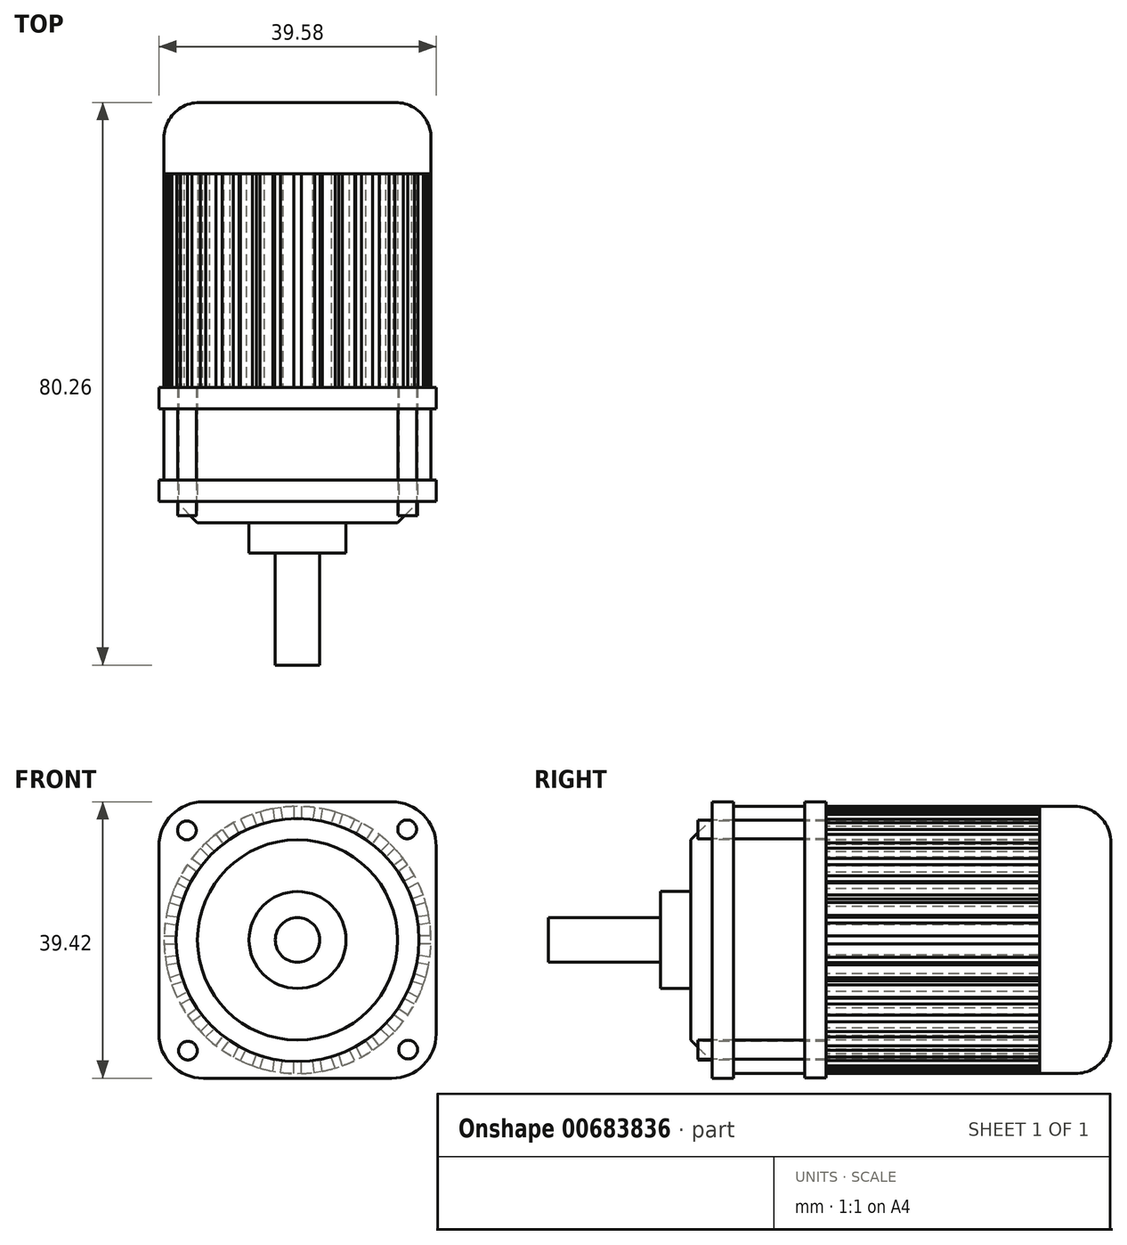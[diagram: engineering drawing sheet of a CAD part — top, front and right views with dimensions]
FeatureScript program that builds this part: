
annotation { "Feature Type Name" : "Feature", "Feature Type Description" : "" }
export const myFeature = defineFeature(function(context is Context, id is Id, definition is map)
    precondition{}
    {
        {
            var Q0;
            Q0=qCreatedBy(makeId("Front.planeOp"),FACE);
            var sketch = newSketch(context, id + "F0", { "sketchPlane" : qUnion([Q0])});
            skCircle(sketch, "E0", {"center": v(0, 0) * mm, "radius": 19.05 * mm});
            skSolve(sketch);
        }
        {
            var Q0;
            Q0=makeQuery(id+"F0.imprint","IMPRINT",FACE,{"disambiguationData":[TD([[makeQuery(id+"F0.imprint","IMPRINT",EDGE,{"derivedFrom":sQuery(id+"F0.wireOp",EDGE,"E0")}),1.0]])]});
            extrude(context, id + "F1", {"entities" : qUnion([Q0]), "depth" : 15.24 * mm, "offsetDistance" : 25.4 * mm, "hasSecondDirection" : true, "secondDirectionOppositeDirection" : true, "secondDirectionDepth" : 15.24 * mm});
        }
        {
            var Q0;
            Q0=makeQuery(id+"F1.opExtrude","CAP_FACE",FACE,{"disambiguationData":[OSD([sQuery(id+"F0.wireOp",EDGE,"E0")])],"isStart":false});
            var sketch = newSketch(context, id + "F2", { "sketchPlane" : qUnion([Q0])});
            skLineSegment(sketch, "E1.bottom", {"start": v(-0.55, 19.72) * mm, "end": v(0.56, 19.72) * mm});
            skLineSegment(sketch, "E1.top", {"start": v(-0.55, 17.23) * mm, "end": v(0.56, 17.23) * mm});
            skLineSegment(sketch, "E1.left", {"start": v(-0.55, 19.72) * mm, "end": v(-0.55, 17.23) * mm});
            skLineSegment(sketch, "E1.right", {"start": v(0.56, 19.72) * mm, "end": v(0.56, 17.23) * mm});
            skLineSegment(sketch, "E2.1.0", {"start": v(3.64, 19.39) * mm, "end": v(3.25, 16.94) * mm});
            skLineSegment(sketch, "E2.1.1", {"start": v(2.54, 19.56) * mm, "end": v(3.64, 19.39) * mm});
            skLineSegment(sketch, "E2.1.2", {"start": v(2.15, 17.1) * mm, "end": v(3.25, 16.94) * mm});
            skLineSegment(sketch, "E2.1.3", {"start": v(2.54, 19.56) * mm, "end": v(2.15, 17.1) * mm});
            skLineSegment(sketch, "E2.2.0", {"start": v(6.62, 18.58) * mm, "end": v(5.86, 16.22) * mm});
            skLineSegment(sketch, "E2.2.1", {"start": v(5.57, 18.92) * mm, "end": v(6.62, 18.58) * mm});
            skLineSegment(sketch, "E2.2.2", {"start": v(4.8, 16.56) * mm, "end": v(5.86, 16.22) * mm});
            skLineSegment(sketch, "E2.2.3", {"start": v(5.57, 18.92) * mm, "end": v(4.8, 16.56) * mm});
            skLineSegment(sketch, "E2.3.0", {"start": v(9.45, 17.31) * mm, "end": v(8.32, 15.1) * mm});
            skLineSegment(sketch, "E2.3.1", {"start": v(8.46, 17.82) * mm, "end": v(9.45, 17.31) * mm});
            skLineSegment(sketch, "E2.3.2", {"start": v(7.33, 15.6) * mm, "end": v(8.32, 15.1) * mm});
            skLineSegment(sketch, "E2.3.3", {"start": v(8.46, 17.82) * mm, "end": v(7.33, 15.6) * mm});
            skLineSegment(sketch, "E2.4.0", {"start": v(12.04, 15.62) * mm, "end": v(10.58, 13.62) * mm});
            skLineSegment(sketch, "E2.4.1", {"start": v(11.14, 16.28) * mm, "end": v(12.04, 15.62) * mm});
            skLineSegment(sketch, "E2.4.2", {"start": v(9.68, 14.27) * mm, "end": v(10.58, 13.62) * mm});
            skLineSegment(sketch, "E2.4.3", {"start": v(11.14, 16.28) * mm, "end": v(9.68, 14.27) * mm});
            skLineSegment(sketch, "E2.5.0", {"start": v(14.34, 13.55) * mm, "end": v(12.58, 11.8) * mm});
            skLineSegment(sketch, "E2.5.1", {"start": v(13.55, 14.33) * mm, "end": v(14.34, 13.55) * mm});
            skLineSegment(sketch, "E2.5.2", {"start": v(11.8, 12.58) * mm, "end": v(12.58, 11.8) * mm});
            skLineSegment(sketch, "E2.5.3", {"start": v(13.55, 14.33) * mm, "end": v(11.8, 12.58) * mm});
            skLineSegment(sketch, "E2.6.0", {"start": v(16.28, 11.14) * mm, "end": v(14.27, 9.68) * mm});
            skLineSegment(sketch, "E2.6.1", {"start": v(15.63, 12.04) * mm, "end": v(16.28, 11.14) * mm});
            skLineSegment(sketch, "E2.6.2", {"start": v(13.62, 10.58) * mm, "end": v(14.27, 9.68) * mm});
            skLineSegment(sketch, "E2.6.3", {"start": v(15.63, 12.04) * mm, "end": v(13.62, 10.58) * mm});
            skLineSegment(sketch, "E2.7.0", {"start": v(17.82, 8.45) * mm, "end": v(15.6, 7.33) * mm});
            skLineSegment(sketch, "E2.7.1", {"start": v(17.32, 9.44) * mm, "end": v(17.82, 8.45) * mm});
            skLineSegment(sketch, "E2.7.2", {"start": v(15.1, 8.32) * mm, "end": v(15.6, 7.33) * mm});
            skLineSegment(sketch, "E2.7.3", {"start": v(17.32, 9.44) * mm, "end": v(15.1, 8.32) * mm});
            skLineSegment(sketch, "E2.8.0", {"start": v(18.92, 5.56) * mm, "end": v(16.56, 4.8) * mm});
            skLineSegment(sketch, "E2.8.1", {"start": v(18.58, 6.62) * mm, "end": v(18.92, 5.56) * mm});
            skLineSegment(sketch, "E2.8.2", {"start": v(16.22, 5.85) * mm, "end": v(16.56, 4.8) * mm});
            skLineSegment(sketch, "E2.8.3", {"start": v(18.58, 6.62) * mm, "end": v(16.22, 5.85) * mm});
            skLineSegment(sketch, "E2.9.0", {"start": v(19.56, 2.53) * mm, "end": v(17.11, 2.14) * mm});
            skLineSegment(sketch, "E2.9.1", {"start": v(19.39, 3.63) * mm, "end": v(19.56, 2.53) * mm});
            skLineSegment(sketch, "E2.9.2", {"start": v(16.94, 3.24) * mm, "end": v(17.11, 2.14) * mm});
            skLineSegment(sketch, "E2.9.3", {"start": v(19.39, 3.63) * mm, "end": v(16.94, 3.24) * mm});
            skLineSegment(sketch, "E2.10.0", {"start": v(19.72, -0.56) * mm, "end": v(17.23, -0.56) * mm});
            skLineSegment(sketch, "E2.10.1", {"start": v(19.72, 0.55) * mm, "end": v(19.72, -0.56) * mm});
            skLineSegment(sketch, "E2.10.2", {"start": v(17.23, 0.55) * mm, "end": v(17.23, -0.56) * mm});
            skLineSegment(sketch, "E2.10.3", {"start": v(19.72, 0.55) * mm, "end": v(17.23, 0.55) * mm});
            skLineSegment(sketch, "E2.11.0", {"start": v(19.39, -3.64) * mm, "end": v(16.94, -3.25) * mm});
            skLineSegment(sketch, "E2.11.1", {"start": v(19.56, -2.54) * mm, "end": v(19.39, -3.64) * mm});
            skLineSegment(sketch, "E2.11.2", {"start": v(17.1, -2.15) * mm, "end": v(16.94, -3.25) * mm});
            skLineSegment(sketch, "E2.11.3", {"start": v(19.56, -2.54) * mm, "end": v(17.1, -2.15) * mm});
            skLineSegment(sketch, "E2.12.0", {"start": v(18.58, -6.62) * mm, "end": v(16.22, -5.86) * mm});
            skLineSegment(sketch, "E2.12.1", {"start": v(18.92, -5.57) * mm, "end": v(18.58, -6.62) * mm});
            skLineSegment(sketch, "E2.12.2", {"start": v(16.56, -4.8) * mm, "end": v(16.22, -5.86) * mm});
            skLineSegment(sketch, "E2.12.3", {"start": v(18.92, -5.57) * mm, "end": v(16.56, -4.8) * mm});
            skLineSegment(sketch, "E2.13.0", {"start": v(17.31, -9.45) * mm, "end": v(15.1, -8.32) * mm});
            skLineSegment(sketch, "E2.13.1", {"start": v(17.82, -8.46) * mm, "end": v(17.31, -9.45) * mm});
            skLineSegment(sketch, "E2.13.2", {"start": v(15.6, -7.33) * mm, "end": v(15.1, -8.32) * mm});
            skLineSegment(sketch, "E2.13.3", {"start": v(17.82, -8.46) * mm, "end": v(15.6, -7.33) * mm});
            skLineSegment(sketch, "E2.14.0", {"start": v(15.62, -12.04) * mm, "end": v(13.62, -10.58) * mm});
            skLineSegment(sketch, "E2.14.1", {"start": v(16.28, -11.14) * mm, "end": v(15.62, -12.04) * mm});
            skLineSegment(sketch, "E2.14.2", {"start": v(14.27, -9.68) * mm, "end": v(13.62, -10.58) * mm});
            skLineSegment(sketch, "E2.14.3", {"start": v(16.28, -11.14) * mm, "end": v(14.27, -9.68) * mm});
            skLineSegment(sketch, "E2.15.0", {"start": v(13.55, -14.34) * mm, "end": v(11.8, -12.58) * mm});
            skLineSegment(sketch, "E2.15.1", {"start": v(14.33, -13.55) * mm, "end": v(13.55, -14.34) * mm});
            skLineSegment(sketch, "E2.15.2", {"start": v(12.58, -11.8) * mm, "end": v(11.8, -12.58) * mm});
            skLineSegment(sketch, "E2.15.3", {"start": v(14.33, -13.55) * mm, "end": v(12.58, -11.8) * mm});
            skLineSegment(sketch, "E2.16.0", {"start": v(11.14, -16.28) * mm, "end": v(9.68, -14.27) * mm});
            skLineSegment(sketch, "E2.16.1", {"start": v(12.04, -15.63) * mm, "end": v(11.14, -16.28) * mm});
            skLineSegment(sketch, "E2.16.2", {"start": v(10.58, -13.62) * mm, "end": v(9.68, -14.27) * mm});
            skLineSegment(sketch, "E2.16.3", {"start": v(12.04, -15.63) * mm, "end": v(10.58, -13.62) * mm});
            skLineSegment(sketch, "E2.17.0", {"start": v(8.45, -17.82) * mm, "end": v(7.33, -15.6) * mm});
            skLineSegment(sketch, "E2.17.1", {"start": v(9.44, -17.32) * mm, "end": v(8.45, -17.82) * mm});
            skLineSegment(sketch, "E2.17.2", {"start": v(8.32, -15.1) * mm, "end": v(7.33, -15.6) * mm});
            skLineSegment(sketch, "E2.17.3", {"start": v(9.44, -17.32) * mm, "end": v(8.32, -15.1) * mm});
            skLineSegment(sketch, "E2.18.0", {"start": v(5.56, -18.92) * mm, "end": v(4.8, -16.56) * mm});
            skLineSegment(sketch, "E2.18.1", {"start": v(6.62, -18.58) * mm, "end": v(5.56, -18.92) * mm});
            skLineSegment(sketch, "E2.18.2", {"start": v(5.85, -16.22) * mm, "end": v(4.8, -16.56) * mm});
            skLineSegment(sketch, "E2.18.3", {"start": v(6.62, -18.58) * mm, "end": v(5.85, -16.22) * mm});
            skLineSegment(sketch, "E2.19.0", {"start": v(2.53, -19.56) * mm, "end": v(2.14, -17.11) * mm});
            skLineSegment(sketch, "E2.19.1", {"start": v(3.63, -19.39) * mm, "end": v(2.53, -19.56) * mm});
            skLineSegment(sketch, "E2.19.2", {"start": v(3.24, -16.94) * mm, "end": v(2.14, -17.11) * mm});
            skLineSegment(sketch, "E2.19.3", {"start": v(3.63, -19.39) * mm, "end": v(3.24, -16.94) * mm});
            skLineSegment(sketch, "E2.20.0", {"start": v(-0.56, -19.72) * mm, "end": v(-0.56, -17.23) * mm});
            skLineSegment(sketch, "E2.20.1", {"start": v(0.55, -19.72) * mm, "end": v(-0.56, -19.72) * mm});
            skLineSegment(sketch, "E2.20.2", {"start": v(0.55, -17.23) * mm, "end": v(-0.56, -17.23) * mm});
            skLineSegment(sketch, "E2.20.3", {"start": v(0.55, -19.72) * mm, "end": v(0.55, -17.23) * mm});
            skLineSegment(sketch, "E2.21.0", {"start": v(-3.64, -19.39) * mm, "end": v(-3.25, -16.94) * mm});
            skLineSegment(sketch, "E2.21.1", {"start": v(-2.54, -19.56) * mm, "end": v(-3.64, -19.39) * mm});
            skLineSegment(sketch, "E2.21.2", {"start": v(-2.15, -17.1) * mm, "end": v(-3.25, -16.94) * mm});
            skLineSegment(sketch, "E2.21.3", {"start": v(-2.54, -19.56) * mm, "end": v(-2.15, -17.1) * mm});
            skLineSegment(sketch, "E2.22.0", {"start": v(-6.62, -18.58) * mm, "end": v(-5.86, -16.22) * mm});
            skLineSegment(sketch, "E2.22.1", {"start": v(-5.57, -18.92) * mm, "end": v(-6.62, -18.58) * mm});
            skLineSegment(sketch, "E2.22.2", {"start": v(-4.8, -16.56) * mm, "end": v(-5.86, -16.22) * mm});
            skLineSegment(sketch, "E2.22.3", {"start": v(-5.57, -18.92) * mm, "end": v(-4.8, -16.56) * mm});
            skLineSegment(sketch, "E2.23.0", {"start": v(-9.45, -17.31) * mm, "end": v(-8.32, -15.1) * mm});
            skLineSegment(sketch, "E2.23.1", {"start": v(-8.46, -17.82) * mm, "end": v(-9.45, -17.31) * mm});
            skLineSegment(sketch, "E2.23.2", {"start": v(-7.33, -15.6) * mm, "end": v(-8.32, -15.1) * mm});
            skLineSegment(sketch, "E2.23.3", {"start": v(-8.46, -17.82) * mm, "end": v(-7.33, -15.6) * mm});
            skLineSegment(sketch, "E2.24.0", {"start": v(-12.04, -15.62) * mm, "end": v(-10.58, -13.62) * mm});
            skLineSegment(sketch, "E2.24.1", {"start": v(-11.14, -16.28) * mm, "end": v(-12.04, -15.62) * mm});
            skLineSegment(sketch, "E2.24.2", {"start": v(-9.68, -14.27) * mm, "end": v(-10.58, -13.62) * mm});
            skLineSegment(sketch, "E2.24.3", {"start": v(-11.14, -16.28) * mm, "end": v(-9.68, -14.27) * mm});
            skLineSegment(sketch, "E2.25.0", {"start": v(-14.34, -13.55) * mm, "end": v(-12.58, -11.8) * mm});
            skLineSegment(sketch, "E2.25.1", {"start": v(-13.55, -14.33) * mm, "end": v(-14.34, -13.55) * mm});
            skLineSegment(sketch, "E2.25.2", {"start": v(-11.8, -12.58) * mm, "end": v(-12.58, -11.8) * mm});
            skLineSegment(sketch, "E2.25.3", {"start": v(-13.55, -14.33) * mm, "end": v(-11.8, -12.58) * mm});
            skLineSegment(sketch, "E2.26.0", {"start": v(-16.28, -11.14) * mm, "end": v(-14.27, -9.68) * mm});
            skLineSegment(sketch, "E2.26.1", {"start": v(-15.63, -12.04) * mm, "end": v(-16.28, -11.14) * mm});
            skLineSegment(sketch, "E2.26.2", {"start": v(-13.62, -10.58) * mm, "end": v(-14.27, -9.68) * mm});
            skLineSegment(sketch, "E2.26.3", {"start": v(-15.63, -12.04) * mm, "end": v(-13.62, -10.58) * mm});
            skLineSegment(sketch, "E2.27.0", {"start": v(-17.82, -8.45) * mm, "end": v(-15.6, -7.33) * mm});
            skLineSegment(sketch, "E2.27.1", {"start": v(-17.32, -9.44) * mm, "end": v(-17.82, -8.45) * mm});
            skLineSegment(sketch, "E2.27.2", {"start": v(-15.1, -8.32) * mm, "end": v(-15.6, -7.33) * mm});
            skLineSegment(sketch, "E2.27.3", {"start": v(-17.32, -9.44) * mm, "end": v(-15.1, -8.32) * mm});
            skLineSegment(sketch, "E2.28.0", {"start": v(-18.92, -5.56) * mm, "end": v(-16.56, -4.8) * mm});
            skLineSegment(sketch, "E2.28.1", {"start": v(-18.58, -6.62) * mm, "end": v(-18.92, -5.56) * mm});
            skLineSegment(sketch, "E2.28.2", {"start": v(-16.22, -5.85) * mm, "end": v(-16.56, -4.8) * mm});
            skLineSegment(sketch, "E2.28.3", {"start": v(-18.58, -6.62) * mm, "end": v(-16.22, -5.85) * mm});
            skLineSegment(sketch, "E2.29.0", {"start": v(-19.56, -2.53) * mm, "end": v(-17.11, -2.14) * mm});
            skLineSegment(sketch, "E2.29.1", {"start": v(-19.39, -3.63) * mm, "end": v(-19.56, -2.53) * mm});
            skLineSegment(sketch, "E2.29.2", {"start": v(-16.94, -3.24) * mm, "end": v(-17.11, -2.14) * mm});
            skLineSegment(sketch, "E2.29.3", {"start": v(-19.39, -3.63) * mm, "end": v(-16.94, -3.24) * mm});
            skLineSegment(sketch, "E2.30.0", {"start": v(-19.72, 0.56) * mm, "end": v(-17.23, 0.56) * mm});
            skLineSegment(sketch, "E2.30.1", {"start": v(-19.72, -0.55) * mm, "end": v(-19.72, 0.56) * mm});
            skLineSegment(sketch, "E2.30.2", {"start": v(-17.23, -0.55) * mm, "end": v(-17.23, 0.56) * mm});
            skLineSegment(sketch, "E2.30.3", {"start": v(-19.72, -0.55) * mm, "end": v(-17.23, -0.55) * mm});
            skLineSegment(sketch, "E2.31.0", {"start": v(-19.39, 3.64) * mm, "end": v(-16.94, 3.25) * mm});
            skLineSegment(sketch, "E2.31.1", {"start": v(-19.56, 2.54) * mm, "end": v(-19.39, 3.64) * mm});
            skLineSegment(sketch, "E2.31.2", {"start": v(-17.1, 2.15) * mm, "end": v(-16.94, 3.25) * mm});
            skLineSegment(sketch, "E2.31.3", {"start": v(-19.56, 2.54) * mm, "end": v(-17.1, 2.15) * mm});
            skLineSegment(sketch, "E2.32.0", {"start": v(-18.58, 6.62) * mm, "end": v(-16.22, 5.86) * mm});
            skLineSegment(sketch, "E2.32.1", {"start": v(-18.92, 5.57) * mm, "end": v(-18.58, 6.62) * mm});
            skLineSegment(sketch, "E2.32.2", {"start": v(-16.56, 4.8) * mm, "end": v(-16.22, 5.86) * mm});
            skLineSegment(sketch, "E2.32.3", {"start": v(-18.92, 5.57) * mm, "end": v(-16.56, 4.8) * mm});
            skLineSegment(sketch, "E2.33.0", {"start": v(-17.31, 9.45) * mm, "end": v(-15.1, 8.32) * mm});
            skLineSegment(sketch, "E2.33.1", {"start": v(-17.82, 8.46) * mm, "end": v(-17.31, 9.45) * mm});
            skLineSegment(sketch, "E2.33.2", {"start": v(-15.6, 7.33) * mm, "end": v(-15.1, 8.32) * mm});
            skLineSegment(sketch, "E2.33.3", {"start": v(-17.82, 8.46) * mm, "end": v(-15.6, 7.33) * mm});
            skLineSegment(sketch, "E2.34.0", {"start": v(-15.62, 12.04) * mm, "end": v(-13.62, 10.58) * mm});
            skLineSegment(sketch, "E2.34.1", {"start": v(-16.28, 11.14) * mm, "end": v(-15.62, 12.04) * mm});
            skLineSegment(sketch, "E2.34.2", {"start": v(-14.27, 9.68) * mm, "end": v(-13.62, 10.58) * mm});
            skLineSegment(sketch, "E2.34.3", {"start": v(-16.28, 11.14) * mm, "end": v(-14.27, 9.68) * mm});
            skLineSegment(sketch, "E2.35.0", {"start": v(-13.55, 14.34) * mm, "end": v(-11.8, 12.58) * mm});
            skLineSegment(sketch, "E2.35.1", {"start": v(-14.33, 13.55) * mm, "end": v(-13.55, 14.34) * mm});
            skLineSegment(sketch, "E2.35.2", {"start": v(-12.58, 11.8) * mm, "end": v(-11.8, 12.58) * mm});
            skLineSegment(sketch, "E2.35.3", {"start": v(-14.33, 13.55) * mm, "end": v(-12.58, 11.8) * mm});
            skLineSegment(sketch, "E2.36.0", {"start": v(-11.14, 16.28) * mm, "end": v(-9.68, 14.27) * mm});
            skLineSegment(sketch, "E2.36.1", {"start": v(-12.04, 15.63) * mm, "end": v(-11.14, 16.28) * mm});
            skLineSegment(sketch, "E2.36.2", {"start": v(-10.58, 13.62) * mm, "end": v(-9.68, 14.27) * mm});
            skLineSegment(sketch, "E2.36.3", {"start": v(-12.04, 15.63) * mm, "end": v(-10.58, 13.62) * mm});
            skLineSegment(sketch, "E2.37.0", {"start": v(-8.45, 17.82) * mm, "end": v(-7.33, 15.6) * mm});
            skLineSegment(sketch, "E2.37.1", {"start": v(-9.44, 17.32) * mm, "end": v(-8.45, 17.82) * mm});
            skLineSegment(sketch, "E2.37.2", {"start": v(-8.32, 15.1) * mm, "end": v(-7.33, 15.6) * mm});
            skLineSegment(sketch, "E2.37.3", {"start": v(-9.44, 17.32) * mm, "end": v(-8.32, 15.1) * mm});
            skLineSegment(sketch, "E2.38.0", {"start": v(-5.56, 18.92) * mm, "end": v(-4.8, 16.56) * mm});
            skLineSegment(sketch, "E2.38.1", {"start": v(-6.62, 18.58) * mm, "end": v(-5.56, 18.92) * mm});
            skLineSegment(sketch, "E2.38.2", {"start": v(-5.85, 16.22) * mm, "end": v(-4.8, 16.56) * mm});
            skLineSegment(sketch, "E2.38.3", {"start": v(-6.62, 18.58) * mm, "end": v(-5.85, 16.22) * mm});
            skLineSegment(sketch, "E2.39.0", {"start": v(-2.53, 19.56) * mm, "end": v(-2.14, 17.11) * mm});
            skLineSegment(sketch, "E2.39.1", {"start": v(-3.63, 19.39) * mm, "end": v(-2.53, 19.56) * mm});
            skLineSegment(sketch, "E2.39.2", {"start": v(-3.24, 16.94) * mm, "end": v(-2.14, 17.11) * mm});
            skLineSegment(sketch, "E2.39.3", {"start": v(-3.63, 19.39) * mm, "end": v(-3.24, 16.94) * mm});
            skPoint(sketch, "E2.center", {"position": v(0, 0) * mm});
            skLineSegment(sketch, "E2.anchor1", {"start": v(0, 0) * mm, "end": v(0.56, 17.23) * mm, "construction": true});
            skLineSegment(sketch, "E2.anchor2", {"start": v(0, 0) * mm, "end": v(-2.14, 17.11) * mm, "construction": true});
            skSolve(sketch);
        }
        {
            var Q0;
            Q0 = qSketchRegion(id + "F2", true);
            extrude(context, id + "F3", {"entities" : qUnion([Q0]), "operationType" : NewBodyOperationType.REMOVE, "oppositeDirection" : true, "depth" : 35.56 * mm, "offsetDistance" : 25.4 * mm});
        }
        {
            var Q0;
            Q0=makeQuery(id+"F1.opExtrude","CAP_FACE",FACE,{"disambiguationData":[OSD([sQuery(id+"F0.wireOp",EDGE,"E0")])],"isStart":true});
            var sketch = newSketch(context, id + "F4", { "sketchPlane" : qUnion([Q0])});
            skCircle(sketch, "E3", {"center": v(0, 0) * mm, "radius": 19.05 * mm});
            skSolve(sketch);
        }
        {
            var Q0;
            Q0 = qSketchRegion(id + "F4", true);
            extrude(context, id + "F5", {"entities" : qUnion([Q0]), "depth" : 10.16 * mm, "offsetDistance" : 25.4 * mm});
        }
        {
            var Q0;
            Q0=makeQuery(id+"F5.opExtrude","CAP_FACE",FACE,{"disambiguationData":[OSD([sQuery(id+"F4.wireOp",EDGE,"E3")])],"isStart":false});
            fillet(context, id + "F6", {"entities" : qUnion([Q0]), "radius" : 5.08 * mm, "tangentPropagation" : true, "allowEdgeOverflow" : false});
        }
        {
            var Q0;
            Q0=makeQuery(id+"F1.opExtrude","CAP_FACE",FACE,{"disambiguationData":[OSD([sQuery(id+"F0.wireOp",EDGE,"E0")])],"isStart":false});
            var sketch = newSketch(context, id + "F7", { "sketchPlane" : qUnion([Q0])});
            skLineSegment(sketch, "E4.bottom", {"start": v(13.43, -19.69) * mm, "end": v(-13.43, -19.69) * mm});
            skLineSegment(sketch, "E4.top", {"start": v(13.43, 19.69) * mm, "end": v(-13.43, 19.69) * mm});
            skLineSegment(sketch, "E4.left", {"start": v(19.78, -13.34) * mm, "end": v(19.78, 13.34) * mm});
            skLineSegment(sketch, "E4.right", {"start": v(-19.78, -13.34) * mm, "end": v(-19.78, 13.34) * mm});
            skPoint(sketch, "E4.middle", {"position": v(0, 0) * mm});
            skPoint(sketch, "E5.visualSharp", {"position": v(-19.78, 19.69) * mm});
            skArc(sketch, "E5.filletArc", {"start": v(-13.43, 19.69) * mm, "mid": v(-17.92, 17.83) * mm, "end": v(-19.78, 13.34) * mm});
            skPoint(sketch, "E6.visualSharp", {"position": v(19.78, 19.69) * mm});
            skArc(sketch, "E6.filletArc", {"start": v(19.78, 13.34) * mm, "mid": v(17.92, 17.83) * mm, "end": v(13.43, 19.69) * mm});
            skPoint(sketch, "E7.visualSharp", {"position": v(-19.78, -19.69) * mm});
            skArc(sketch, "E7.filletArc", {"start": v(-19.78, -13.34) * mm, "mid": v(-17.92, -17.83) * mm, "end": v(-13.43, -19.69) * mm});
            skPoint(sketch, "E8.visualSharp", {"position": v(19.78, -19.69) * mm});
            skArc(sketch, "E8.filletArc", {"start": v(13.43, -19.69) * mm, "mid": v(17.92, -17.83) * mm, "end": v(19.78, -13.34) * mm});
            skSolve(sketch);
        }
        {
            var Q0;
            Q0 = qSketchRegion(id + "F7", true);
            extrude(context, id + "F8", {"entities" : qUnion([Q0]), "depth" : 3.05 * mm, "offsetDistance" : 25.4 * mm});
        }
        {
            var Q0;
            Q0=makeQuery(id+"F8.opExtrude","CAP_FACE",FACE,{"disambiguationData":[OSD([sQuery(id+"F7.wireOp",EDGE,"E4.bottom"),sQuery(id+"F7.wireOp",EDGE,"E4.top"),sQuery(id+"F7.wireOp",EDGE,"E4.left"),sQuery(id+"F7.wireOp",EDGE,"E4.right"),sQuery(id+"F7.wireOp",EDGE,"E5.filletArc"),sQuery(id+"F7.wireOp",EDGE,"E6.filletArc"),sQuery(id+"F7.wireOp",EDGE,"E7.filletArc"),sQuery(id+"F7.wireOp",EDGE,"E8.filletArc")])],"isStart":false});
            var sketch = newSketch(context, id + "F9", { "sketchPlane" : qUnion([Q0])});
            skCircle(sketch, "E9", {"center": v(0, 0) * mm, "radius": 19.05 * mm});
            skSolve(sketch);
        }
        {
            var Q0;
            Q0=makeQuery(id+"F9.imprint","IMPRINT",FACE,{"disambiguationData":[TD([[makeQuery(id+"F9.imprint","IMPRINT",EDGE,{"derivedFrom":sQuery(id+"F9.wireOp",EDGE,"E9")}),1.0]])]});
            extrude(context, id + "F10", {"entities" : qUnion([Q0]), "depth" : 10.16 * mm, "offsetDistance" : 25.4 * mm});
        }
        {
            var Q0;
            Q0=makeQuery(id+"F10.opExtrude","CAP_FACE",FACE,{"disambiguationData":[OSD([sQuery(id+"F9.wireOp",EDGE,"E9")])],"isStart":false});
            var sketch = newSketch(context, id + "F11", { "sketchPlane" : qUnion([Q0])});
            skLineSegment(sketch, "E10.bottom", {"start": v(13.44, -19.71) * mm, "end": v(-13.44, -19.71) * mm});
            skLineSegment(sketch, "E10.top", {"start": v(13.44, 19.71) * mm, "end": v(-13.44, 19.71) * mm});
            skLineSegment(sketch, "E10.left", {"start": v(19.8, -13.36) * mm, "end": v(19.8, 13.36) * mm});
            skLineSegment(sketch, "E10.right", {"start": v(-19.8, -13.36) * mm, "end": v(-19.8, 13.36) * mm});
            skPoint(sketch, "E10.middle", {"position": v(0, 0) * mm});
            skPoint(sketch, "E11.visualSharp", {"position": v(-19.8, 19.71) * mm});
            skArc(sketch, "E11.filletArc", {"start": v(-13.44, 19.71) * mm, "mid": v(-17.93, 17.85) * mm, "end": v(-19.8, 13.36) * mm});
            skPoint(sketch, "E12.visualSharp", {"position": v(19.8, 19.71) * mm});
            skArc(sketch, "E12.filletArc", {"start": v(19.8, 13.36) * mm, "mid": v(17.93, 17.85) * mm, "end": v(13.44, 19.71) * mm});
            skPoint(sketch, "E13.visualSharp", {"position": v(19.8, -19.71) * mm});
            skArc(sketch, "E13.filletArc", {"start": v(13.44, -19.71) * mm, "mid": v(17.93, -17.85) * mm, "end": v(19.8, -13.36) * mm});
            skPoint(sketch, "E14.visualSharp", {"position": v(-19.8, -19.71) * mm});
            skArc(sketch, "E14.filletArc", {"start": v(-19.8, -13.36) * mm, "mid": v(-17.93, -17.85) * mm, "end": v(-13.44, -19.71) * mm});
            skSolve(sketch);
        }
        {
            var Q0;
            Q0 = qSketchRegion(id + "F11", true);
            extrude(context, id + "F12", {"entities" : qUnion([Q0]), "depth" : 3.05 * mm, "offsetDistance" : 25.4 * mm});
        }
        {
            var Q0;
            Q0=makeQuery(id+"F12.opExtrude","CAP_FACE",FACE,{"disambiguationData":[OSD([sQuery(id+"F11.wireOp",EDGE,"E10.bottom"),sQuery(id+"F11.wireOp",EDGE,"E10.top"),sQuery(id+"F11.wireOp",EDGE,"E10.left"),sQuery(id+"F11.wireOp",EDGE,"E10.right"),sQuery(id+"F11.wireOp",EDGE,"E11.filletArc"),sQuery(id+"F11.wireOp",EDGE,"E12.filletArc"),sQuery(id+"F11.wireOp",EDGE,"E13.filletArc"),sQuery(id+"F11.wireOp",EDGE,"E14.filletArc")])],"isStart":false});
            var sketch = newSketch(context, id + "F13", { "sketchPlane" : qUnion([Q0])});
            skCircle(sketch, "E15", {"center": v(0, 0) * mm, "radius": 17.33 * mm});
            skSolve(sketch);
        }
        {
            var Q0;
            Q0=makeQuery(id+"F13.imprint","IMPRINT",FACE,{"disambiguationData":[TD([[makeQuery(id+"F13.imprint","IMPRINT",EDGE,{"derivedFrom":sQuery(id+"F13.wireOp",EDGE,"E15")}),1.0]])]});
            extrude(context, id + "F14", {"entities" : qUnion([Q0]), "operationType" : NewBodyOperationType.ADD, "depth" : 3.05 * mm, "offsetDistance" : 25.4 * mm});
        }
        {
            var Q0;
            Q0=makeQuery(id+"F14.opExtrude","CAP_EDGE",EDGE,{"disambiguationData":[OSD([sQuery(id+"F13.wireOp",EDGE,"E15")])],"isStart":false});
            chamfer(context, id + "F15", {"entities" : qUnion([Q0]), "width" : 3.05 * mm, "tangentPropagation" : true});
        }
        {
            var Q0;
            Q0=makeQuery(id+"F14.opExtrude","CAP_FACE",FACE,{"disambiguationData":[OSD([sQuery(id+"F13.wireOp",EDGE,"E15")])],"isStart":false});
            var sketch = newSketch(context, id + "F16", { "sketchPlane" : qUnion([Q0])});
            skCircle(sketch, "E16", {"center": v(0, 0) * mm, "radius": 6.91 * mm});
            skSolve(sketch);
        }
        {
            var Q0;
            Q0=makeQuery(id+"F16.imprint","IMPRINT",FACE,{"disambiguationData":[TD([[makeQuery(id+"F16.imprint","IMPRINT",EDGE,{"derivedFrom":sQuery(id+"F16.wireOp",EDGE,"E16")}),1.0]])]});
            extrude(context, id + "F17", {"entities" : qUnion([Q0]), "operationType" : NewBodyOperationType.ADD, "depth" : 4.32 * mm, "offsetDistance" : 25.4 * mm});
        }
        {
            var Q0;
            Q0=makeQuery(id+"F17.opExtrude","CAP_FACE",FACE,{"disambiguationData":[OSD([sQuery(id+"F16.wireOp",EDGE,"E16")])],"isStart":false});
            var sketch = newSketch(context, id + "F18", { "sketchPlane" : qUnion([Q0])});
            skCircle(sketch, "E17", {"center": v(0, 0) * mm, "radius": 3.18 * mm});
            skSolve(sketch);
        }
        {
            var Q0;
            Q0=makeQuery(id+"F18.imprint","IMPRINT",FACE,{"disambiguationData":[TD([[makeQuery(id+"F18.imprint","IMPRINT",EDGE,{"derivedFrom":sQuery(id+"F18.wireOp",EDGE,"E17")}),1.0]])]});
            extrude(context, id + "F19", {"entities" : qUnion([Q0]), "depth" : 16 * mm, "offsetDistance" : 25.4 * mm});
        }
        {
            var Q0;
            Q0=makeQuery(id+"F12.opExtrude","CAP_FACE",FACE,{"disambiguationData":[OSD([sQuery(id+"F11.wireOp",EDGE,"E10.bottom"),sQuery(id+"F11.wireOp",EDGE,"E10.top"),sQuery(id+"F11.wireOp",EDGE,"E10.left"),sQuery(id+"F11.wireOp",EDGE,"E10.right"),sQuery(id+"F11.wireOp",EDGE,"E11.filletArc"),sQuery(id+"F11.wireOp",EDGE,"E12.filletArc"),sQuery(id+"F11.wireOp",EDGE,"E13.filletArc"),sQuery(id+"F11.wireOp",EDGE,"E14.filletArc")])],"isStart":false});
            var sketch = newSketch(context, id + "F20", { "sketchPlane" : qUnion([Q0])});
            skCircle(sketch, "E18", {"center": v(15.64, 15.79) * mm, "radius": 1.34 * mm});
            skCircle(sketch, "E19.1.0", {"center": v(15.79, -15.64) * mm, "radius": 1.34 * mm});
            skCircle(sketch, "E19.2.0", {"center": v(-15.64, -15.79) * mm, "radius": 1.34 * mm});
            skCircle(sketch, "E19.3.0", {"center": v(-15.79, 15.64) * mm, "radius": 1.34 * mm});
            skPoint(sketch, "E19.center", {"position": v(0, 0) * mm});
            skLineSegment(sketch, "E19.anchor1", {"start": v(0, 0) * mm, "end": v(15.64, 15.79) * mm, "construction": true});
            skLineSegment(sketch, "E19.anchor2", {"start": v(0, 0) * mm, "end": v(-15.79, 15.64) * mm, "construction": true});
            skSolve(sketch);
        }
        {
            var Q0;
            Q0 = qSketchRegion(id + "F20", true);
            extrude(context, id + "F21", {"entities" : qUnion([Q0]), "oppositeDirection" : true, "depth" : 16.26 * mm, "offsetDistance" : 25.4 * mm, "hasSecondDirection" : true, "secondDirectionOppositeDirection" : false, "secondDirectionDepth" : 2.03 * mm});
        }
    });
